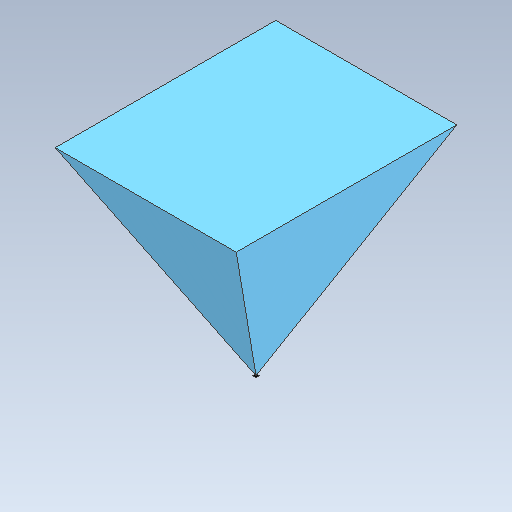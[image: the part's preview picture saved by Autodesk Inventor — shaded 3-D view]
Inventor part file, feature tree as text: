
AUTODESK INVENTOR PART (.ipt)
format: ipt  version: 2020 (Build 240168000, 168)  size: 149,504 bytes
history: native  units: mm
features: extrude x6, sketch x6
ambient origin geometry x8: Origin, YZ Plane, XZ Plane, XY Plane, X Axis, Y Axis, Z Axis, Center Point
bodies: Solid1 (feature_tree)
feature tree (12):
  extrude  "Extrusion1"  Depth=550.0mm
  extrude  "Extrusion2"  TaperAngle=0.0deg  [1 undecoded]
  extrude  "Extrusion3"  Depth=275.0mm
  extrude  "Extrusion4"  TaperAngle=0.0deg  [1 undecoded]
  extrude  "Extrusion5"  Depth=10.0mm
  extrude  "Extrusion6"  Depth=0.1mm
  sketch  "Sketch1"  dims[d0=670.0mm d1=550.0mm]
  sketch  "Sketch5"  dims[d2=630.0mm d3=0.0mm d4=0.0mm d5=0.0mm]
  sketch  "Sketch6"  dims[d6=0.0mm d7=0.0mm d8=275.0mm]
  sketch  "Sketch8"  dims[d9=0.0mm d10=0.0mm d11=0.0mm d12=0.0mm]
  sketch  "Sketch9"  dims[d13=10.0mm d14=10.0mm]
  sketch  "Sketch10"  dims[d15=330.0mm d16=270.0mm d17=0.1mm d18=0.0mm]
note: 2 required parameter values undecoded (feature->parameter linkage not recoverable at this tier; creation-order binding heuristic only, values carry confidence <= 0.55)
